# Revit family: Drain_Floor_Top_Diameter_9_Inch_Zurn-Z554-Medium-Duty-1
name_source: partatom
category: Plumbing Fixtures
units: mm (PartAtom-declared; Revit-internal decimal feet)

## family parameters
Always vertical = Yes
Cut with Voids When Loaded = No
Maintain Annotation Orientation = No
OmniClass Number = 23.45.55.21
OmniClass Title = Drains (Wastes)
Part Type = Normal
Room Calculation Point = No
Round Connector Dimension = Use Radius
Shared = No
Work Plane-Based = No

## types (1)
- Load Family Type Catalog
    Approx. Weight (Lbs) = 21 "
    Assembly Code = D2030300
    Body Height (E) = 4.75 "
    CW Connection = No
    CWFU = 0
    Default Elevation = 25 "
    Description = 9 [229] DIAMETER TOP MEDIUM-DUTY DRAIN
    Frame Dimension = 2 "
    Frame and Grate = Iron - Zurn -Cast - Painted - Blue
    Grate Open Area Sq.in = 9 "
    HW Connection = No
    HWFU = 0
    Inside Plate Radius = 4 "
    Main Material = Iron - Zurn -Cast - Painted - Blue
    Manufacturer = Zurn Water, LLC
    Manufacurer Brand = Zurn
    Model = Z554
    Modified Date = 12/19/2025
    P Trap Primer Connetor = 0.25 "
    Pipe Size_A Inside Radius = 1.034 "
    Pipe Size_A Nominal Radius = 1 "
    Pipe Size_A Outer Radius = 1.188 "
    Product Documentation Link = https://files.zurn.com
    Product Page URL = https://www.zurn.com
    Product data url = https://www.bimobject.com
    Top Diameter = 9 "
    Top Diameter Inner = 8.625 "
    Type Comments = Z554-2 Inch-No Hub Outlet
    URL = www.zurn.com
    Vent Connection = No
    WFU = 1
    Waste Connection = Yes
    Width = 12 "
    Z-Grate = Yes
    ZN-Grate = No

## geometry (parser evidence)
native form markers: Blend x4, Sweep x6
no freeform markers — native parametric forms only
